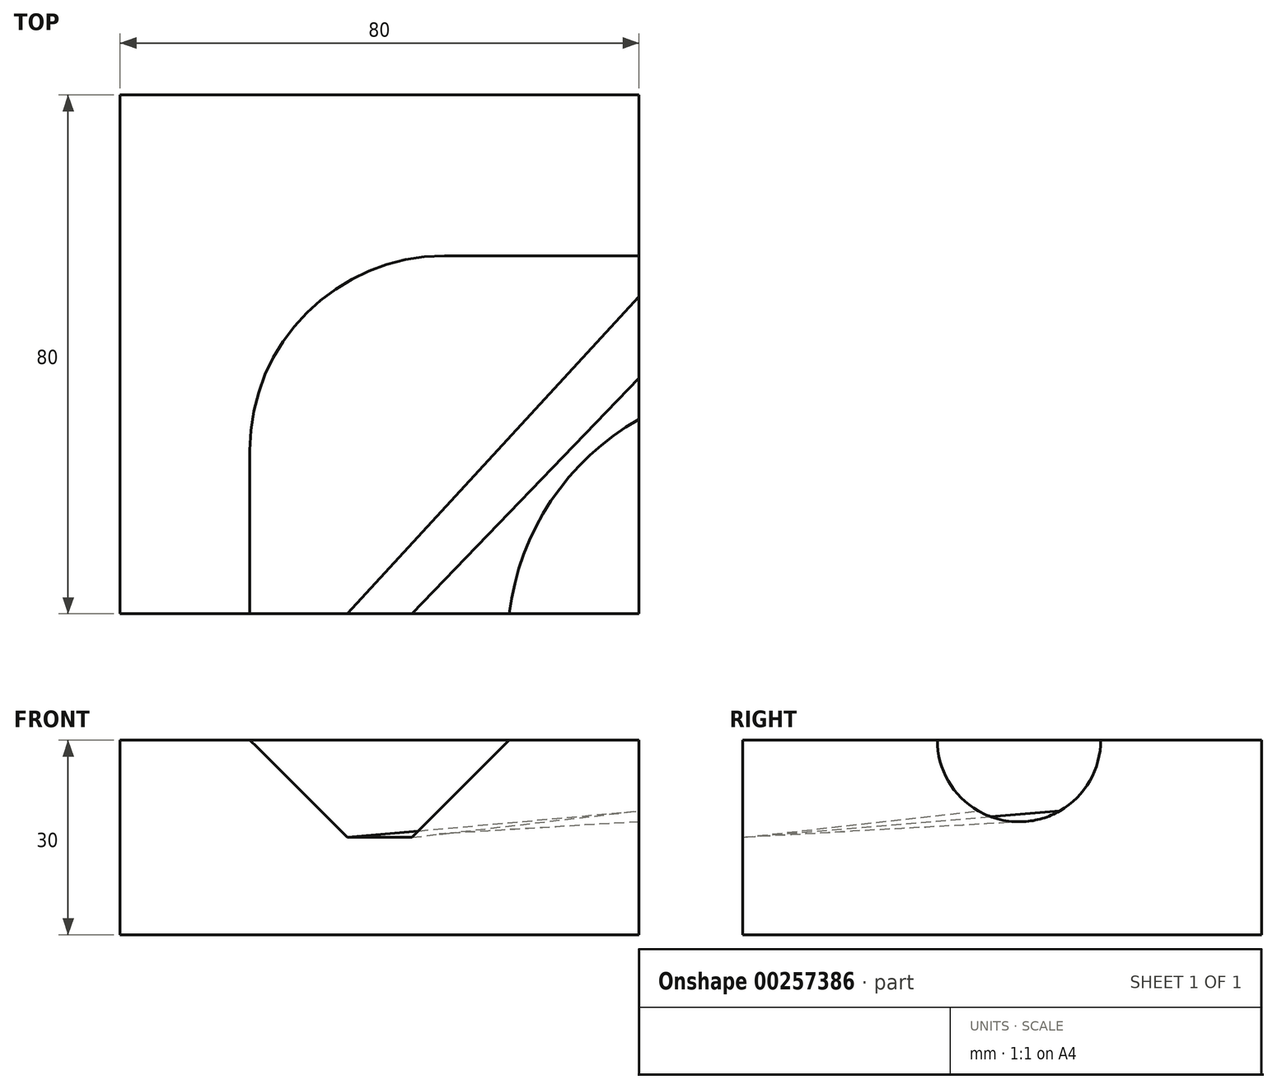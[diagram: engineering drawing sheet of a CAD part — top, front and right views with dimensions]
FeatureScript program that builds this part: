
annotation { "Feature Type Name" : "Feature", "Feature Type Description" : "" }
export const myFeature = defineFeature(function(context is Context, id is Id, definition is map)
    precondition{}
    {
        {
            var Q0;
            Q0=qCreatedBy(makeId("Top.planeOp"),FACE);
            var sketch = newSketch(context, id + "F0", { "sketchPlane" : qUnion([Q0])});
            skLineSegment(sketch, "E0.bottom", {"start": v(0, 0) * mm, "end": v(80, 0) * mm});
            skLineSegment(sketch, "E0.top", {"start": v(0, -80) * mm, "end": v(80, -80) * mm});
            skLineSegment(sketch, "E0.left", {"start": v(0, 0) * mm, "end": v(0, -80) * mm});
            skLineSegment(sketch, "E0.right", {"start": v(80, 0) * mm, "end": v(80, -80) * mm});
            skPoint(sketch, "E1", {"position": v(80, -50) * mm});
            skPoint(sketch, "E2", {"position": v(60, -80) * mm});
            skArc(sketch, "E3", {"start": v(80, -50) * mm, "mid": v(66.43, -62.62) * mm, "end": v(60, -80) * mm});
            skLineSegment(sketch, "E4", {"start": v(20, -80) * mm, "end": v(20, -54.8) * mm});
            skLineSegment(sketch, "E5", {"start": v(80, -24.8) * mm, "end": v(50, -24.8) * mm});
            skArc(sketch, "E6", {"start": v(50, -24.8) * mm, "mid": v(28.79, -33.6) * mm, "end": v(20, -54.8) * mm});
            skSolve(sketch);
        }
        {
            var Q0;
            Q0=qSketchRegion(id+"F0",true);
            extrude(context, id + "F1", {"entities" : qUnion([Q0]), "oppositeDirection" : true, "depth" : 30 * mm});
        }
        {
            var Q0;
            Q0=makeQuery(id+"F1.opExtrude","SWEPT_FACE",FACE,{"disambiguationData":[OSD([sQuery(id+"F0.wireOp",EDGE,"E0.top")])]});
            var sketch = newSketch(context, id + "F2", { "sketchPlane" : qUnion([Q0])});
            skPoint(sketch, "E7.0", {"position": v(20, 0) * mm});
            skPoint(sketch, "E8.0", {"position": v(60, 0) * mm});
            skLineSegment(sketch, "E9", {"start": v(20, 0) * mm, "end": v(35, -15) * mm});
            skLineSegment(sketch, "E10", {"start": v(60, 0) * mm, "end": v(45, -15) * mm});
            skLineSegment(sketch, "E11", {"start": v(20, 0) * mm, "end": v(20, -13.52) * mm, "construction": true});
            skLineSegment(sketch, "E12", {"start": v(35, -15) * mm, "end": v(45, -15) * mm});
            skSolve(sketch);
        }
        {
            var Q0;
            Q0=makeQuery(id+"F1.opExtrude","SWEPT_FACE",FACE,{"disambiguationData":[OSD([sQuery(id+"F0.wireOp",EDGE,"E0.right")])]});
            var sketch = newSketch(context, id + "F3", { "sketchPlane" : qUnion([Q0])});
            skPoint(sketch, "E13.0", {"position": v(-50, 0) * mm});
            skPoint(sketch, "E14.0", {"position": v(-24.8, 0) * mm});
            skLineSegment(sketch, "E15", {"start": v(-24.8, 0) * mm, "end": v(-50, 0) * mm, "construction": true});
            skArc(sketch, "E16", {"start": v(-50, 0) * mm, "mid": v(-37.4, -12.6) * mm, "end": v(-24.8, 0) * mm});
            skSolve(sketch);
        }
        {
            var Q0;
            {var subQ1=sQuery(id+"F0.wireOp",EDGE,"E3");Q0=makeQuery(id+"F0.imprint","IMPRINT",FACE,{"disambiguationData":[TD([[makeQuery(id+"F0.imprint","IMPRINT",EDGE,{"derivedFrom":subQ1}),-1.0]])]});}
            var sketch = newSketch(context, id + "F4", { "sketchPlane" : qUnion([Q0])});
            skLineSegment(sketch, "E17.0.1", {"start": v(80, -24.8) * mm, "end": v(50, -24.8) * mm});
            skArc(sketch, "E17.0.2", {"start": v(50, -24.8) * mm, "mid": v(28.79, -33.6) * mm, "end": v(20, -54.8) * mm});
            skLineSegment(sketch, "E17.0.3", {"start": v(20, -54.8) * mm, "end": v(20, -80) * mm});
            skSolve(sketch);
        }
        {
            var Q1;
            {var subQ0=sQuery(id+"F2.wireOp",EDGE,"E9");Q1=makeQuery(id+"F2.imprint","IMPRINT",FACE,{"disambiguationData":[TD([[makeQuery(id+"F2.imprint","IMPRINT",EDGE,{"derivedFrom":subQ0}),1.0]])]});}
            var Q2;
            {var subQ0=sQuery(id+"F3.wireOp",EDGE,"E16");Q2=makeQuery(id+"F3.imprint","IMPRINT",FACE,{"disambiguationData":[TD([[makeQuery(id+"F3.imprint","IMPRINT",EDGE,{"derivedFrom":subQ0}),1.0]])]});}
            var Q3;
            Q3 = qConstructionFilter(qBodyType(qCreatedBy(id + "F4" ,EDGE), BodyType.WIRE), ConstructionObject.NO);
            var Q4;
            Q4=sQuery(id+"F0.wireOp",EDGE,"E3");
            loft(context, id + "F5", {"operationType" : NewBodyOperationType.REMOVE, "addGuides" : true, "sheetProfilesArray" : [{ "sheetProfileEntities" : qUnion([Q1]) }, { "sheetProfileEntities" : qUnion([Q2]) }], "guidesArray" : [{ "guideEntities" : qUnion([Q3]), "guideDerivativeType" : LoftGuideDerivativeType.DEFAULT, "guideDerivativeMagnitude" : 1 }, { "guideEntities" : qUnion([Q4]), "guideDerivativeType" : LoftGuideDerivativeType.DEFAULT, "guideDerivativeMagnitude" : 1 }]});
        }
    });
